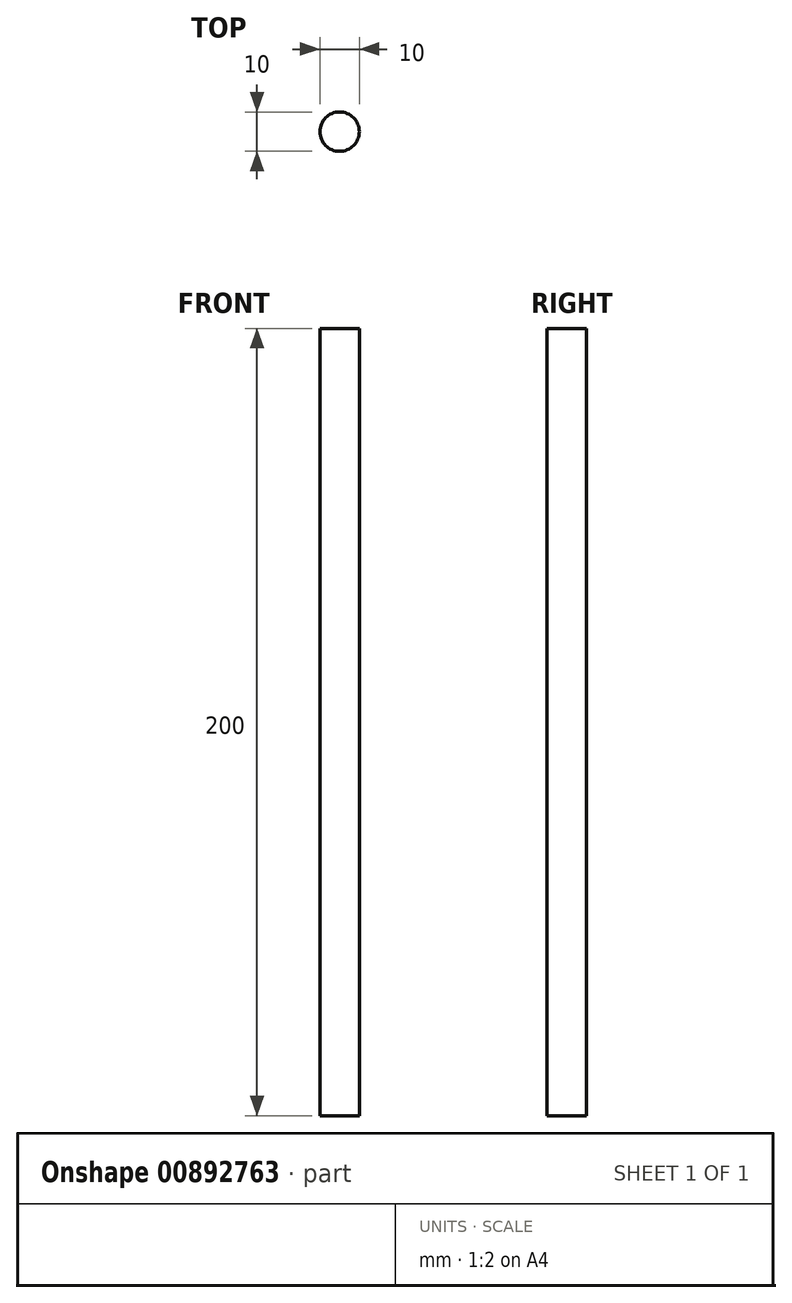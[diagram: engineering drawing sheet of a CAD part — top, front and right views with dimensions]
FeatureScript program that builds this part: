
annotation { "Feature Type Name" : "Feature", "Feature Type Description" : "" }
export const myFeature = defineFeature(function(context is Context, id is Id, definition is map)
    precondition{}
    {
        {
            var Q0;
            Q0=qCreatedBy(makeId("Top.planeOp"),FACE);
            var sketch = newSketch(context, id + "F0", { "sketchPlane" : qUnion([Q0])});
            skCircle(sketch, "E0", {"center": v(0, 0) * mm, "radius": 5 * mm});
            skSolve(sketch);
        }
        {
            var Q0;
            Q0=makeQuery(id+"F0.imprint","IMPRINT",FACE,{"disambiguationData":[TD([[makeQuery(id+"F0.imprint","IMPRINT",EDGE,{"derivedFrom":sQuery(id+"F0.wireOp",EDGE,"E0")}),1.0]])]});
            extrude(context, id + "F1", {"entities" : qUnion([Q0]), "depth" : 200 * mm, "offsetDistance" : 25 * mm});
        }
    });
